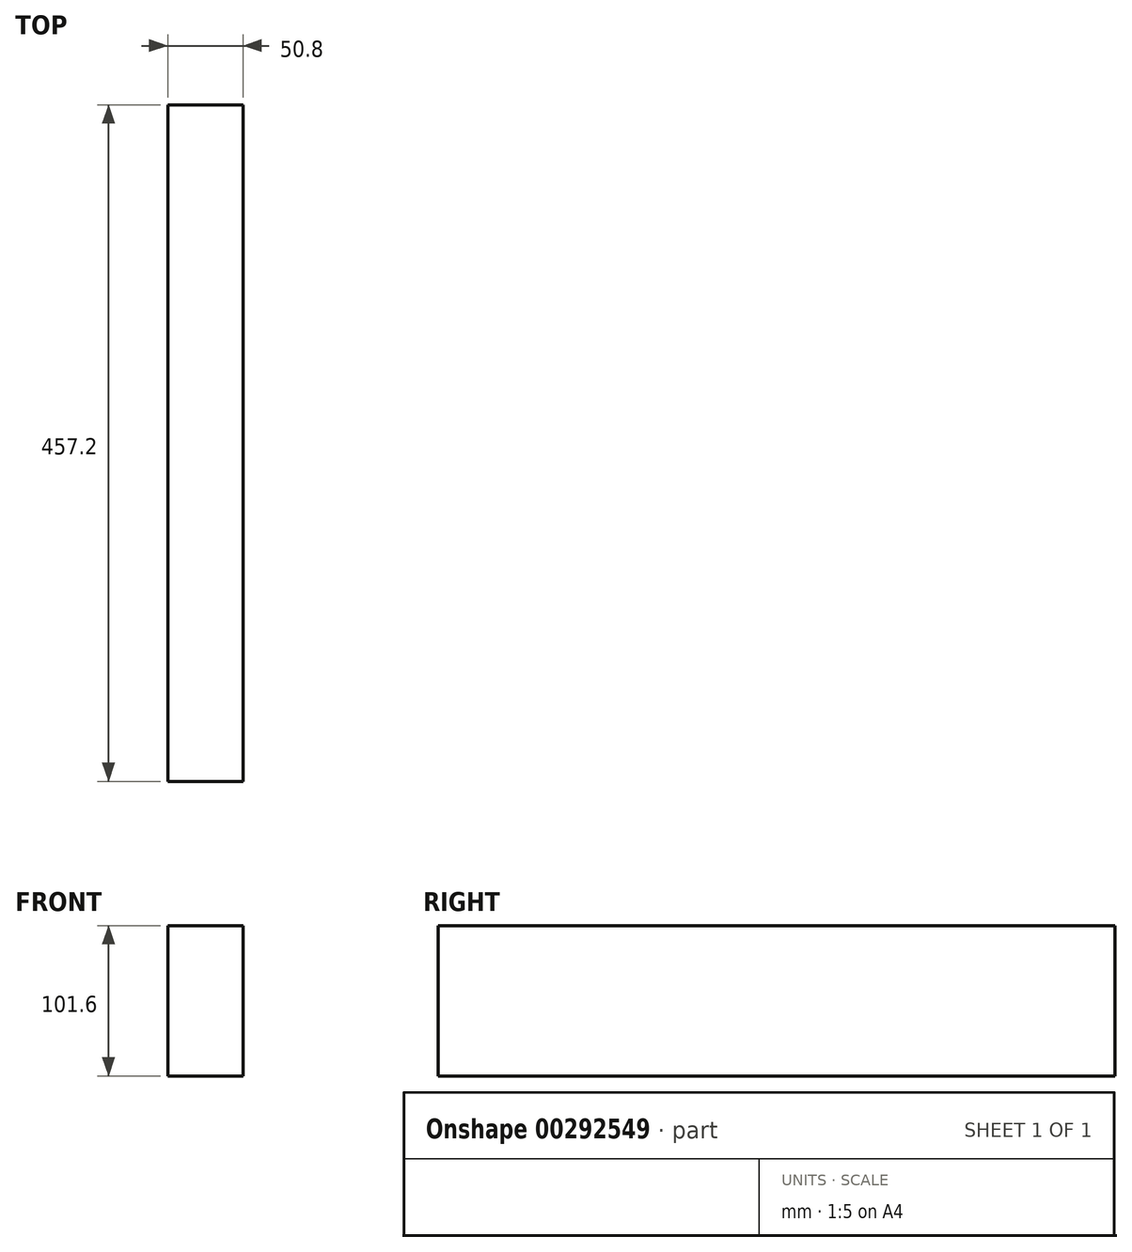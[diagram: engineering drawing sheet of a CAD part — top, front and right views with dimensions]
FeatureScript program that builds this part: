
annotation { "Feature Type Name" : "Feature", "Feature Type Description" : "" }
export const myFeature = defineFeature(function(context is Context, id is Id, definition is map)
    precondition{}
    {
        {
            var Q0;
            Q0=qCreatedBy(makeId("Front.planeOp"),FACE);
            var sketch = newSketch(context, id + "F0", { "sketchPlane" : qUnion([Q0])});
            skLineSegment(sketch, "E0.bottom", {"start": v(0, 0) * mm, "end": v(50.8, 0) * mm});
            skLineSegment(sketch, "E0.top", {"start": v(0, 101.6) * mm, "end": v(50.8, 101.6) * mm});
            skLineSegment(sketch, "E0.left", {"start": v(0, 0) * mm, "end": v(0, 101.6) * mm});
            skLineSegment(sketch, "E0.right", {"start": v(50.8, 0) * mm, "end": v(50.8, 101.6) * mm});
            skSolve(sketch);
        }
        {
            var Q0;
            Q0 = qSketchRegion(id + "F0", true);
            extrude(context, id + "F1", {"entities" : qUnion([Q0]), "depth" : 457.2 * mm});
        }
    });
